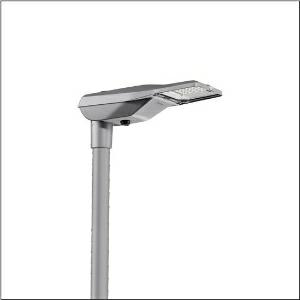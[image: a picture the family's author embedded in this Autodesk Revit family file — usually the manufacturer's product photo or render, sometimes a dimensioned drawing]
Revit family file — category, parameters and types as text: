
# Revit family: streetlight_sl_21_micro___p0_8a_5xe1u33r08db_bf72
name_source: partatom
category: Lighting Fixtures
units: mm (PartAtom-declared; Revit-internal decimal feet)

## family parameters
Cut with Voids When Loaded = No
Host = Face
Light Source = No
Part Type = Normal
Room Calculation Point = No
Round Connector Dimension = Use Diameter
Shared = No

## types (1)
- --- (1 x LED, 5040 lm, 39.1 W, 3000K)
    Apparent Load = 39 VA
    CIE Flux Codes = 33 69 96 100 100
    Color Rendering = 70
    Color Temperature = 3000K
    Default Elevation = 1800 mm
    Description = Streetlight SL 21 micro, mast luminaire, primary light control with lens, of PMMA, primary optical cover: cover, of toughened safety glass, transparent, light distribution: P0.8a, light emission: direct distribution, primary light characteristic: asymmetric, installation type: post-top, side-entry, LED, High Power LED, rated luminous flux: 5.040lm, luminous efficacy: 129lm/W, light colour: 730, colour temperature: 3000K, control gear: D4i, control: pre-setting: logarithmic dimming characteristic, flexible luminous flux parameterisation, time-dependent luminous flux control, constant luminous flux control, overheat protection, mains connection: 220..240V, AC, 50/60Hz, start of lifetime: 39W, end of service life: 41W, reduction: 18W, luminaire housing, of diecast aluminium, powder-coated, SITECO metallic grey (DB 702S), corrosivity category C5 high according to DIN EN ISO 12944, multi-level sealing system, sealing non-destructively replaceable, inclination adjustable: 0°, 5°, 10°, 15°, please order mast flange separately, length: 528mm, width: 235mm, height: 110mm, mast flange for spigot size: 42mm (side-entry): 5XC10008XM4, 60/48mm (side-entry/post-top): 5XC10108XM2, 76/60mm (side-entry/post-top): 5XC10108XM1, Smart Interface below, protection rating (complete): IP66, insulation class (complete): insulation class II (safety insulation), certification: CE, ENEC, ENEC+, VDE, impact resistance: IK10, permissible operating ambient temperature for outdoor applications: -40..+50°C, standard-compliant lighting for roads and squares, packaging unit: 1 piece

Light Distribution: P0.8a
    Height = 110 mm
    Lamp = 1 x LED
    Lamp Light Flux = 5040 lm
    Lamp Power = 39.1 W
    Lamp count = 1
    Length = 528 mm
    Luminous efficacy = 129 lm/W
    Manufacturer = Siteco
    ModVariant = No
    Model = 5XE1U33R08DB
    Number of Poles = 1
    OnlyDefault = Yes
    Power Factor = 1
    Product Name = Streetlight SL 21 micro | P0.8a
    Product group = mast luminaire | pylon top
    ProductGroupID = 6100
    Protection Class = Protection class II
    Protection Degree = IP 66
    RLX_Detail_Level = 1
    RLX_Emergency_Light_Flux = 0 lm
    RLX_Emergency_Type = 0
    RLX_Emergency_Type_DB = No
    RlxData = <blob elided: 99089 chars, md5=fedc1171>
    Socket = socket
    Standby Power = 0 W
    System Light Flux = 5040 lm
    System Power = 39 W
    Type Comments = factory setting: luminous flux: 100 % | dim-lin: 254 | 765 mA
    Type Image = l_1277290.jpg
    URL = http://relux.com
    VarID = @adj_080593
    Voltage = 0 V
    Weight = 0.00 kg
    Width = 235 mm

## geometry (parser evidence)
native form markers: Blend x4, Sweep x10
no freeform markers — native parametric forms only
